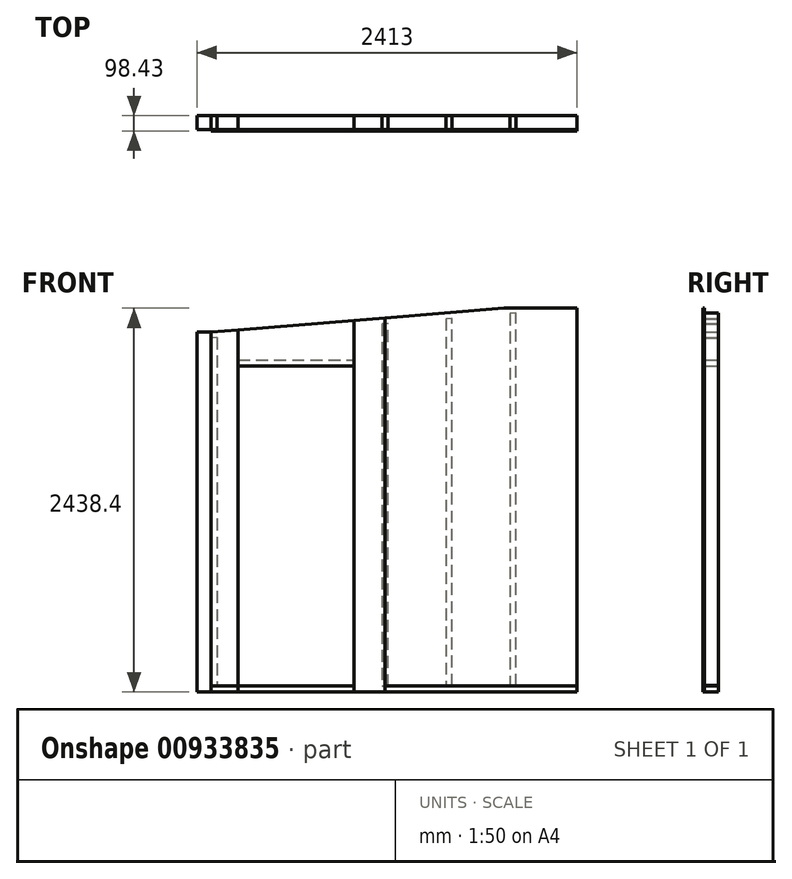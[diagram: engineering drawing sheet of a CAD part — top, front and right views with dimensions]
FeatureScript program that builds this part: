
annotation { "Feature Type Name" : "Feature", "Feature Type Description" : "" }
export const myFeature = defineFeature(function(context is Context, id is Id, definition is map)
    precondition{}
    {
        {
            var Q0;
            Q0=qCreatedBy(makeId("Front.planeOp"),FACE);
            var sketch = newSketch(context, id + "F0", { "sketchPlane" : qUnion([Q0])});
            skLineSegment(sketch, "E0.bottom", {"start": v(1162.05, -1238.25) * mm, "end": v(-1162.05, -1238.25) * mm, "construction": true});
            skLineSegment(sketch, "E0.left", {"start": v(1162.05, -1238.25) * mm, "end": v(1162.05, 1238.25) * mm, "construction": true});
            skPoint(sketch, "E0.middle", {"position": v(0, 0) * mm});
            skLineSegment(sketch, "E1.bottom", {"start": v(-1162.05, -1238.25) * mm, "end": v(1162.05, -1238.25) * mm});
            skLineSegment(sketch, "E1.top", {"start": v(-1162.05, -1200.15) * mm, "end": v(1162.05, -1200.15) * mm});
            skLineSegment(sketch, "E1.left", {"start": v(-1162.05, -1238.25) * mm, "end": v(-1162.05, -1200.15) * mm});
            skLineSegment(sketch, "E1.right", {"start": v(1162.05, -1238.25) * mm, "end": v(1162.05, -1200.15) * mm});
            skLineSegment(sketch, "E2", {"start": v(-1162.05, -1200.15) * mm, "end": v(-1162.05, 1047.75) * mm});
            skLineSegment(sketch, "E3", {"start": v(-1162.05, 1047.75) * mm, "end": v(-1162.05, -1200.15) * mm});
            skLineSegment(sketch, "E4.bottom", {"start": v(-1162.05, 1047.75) * mm, "end": v(-1250.95, 1047.75) * mm});
            skLineSegment(sketch, "E4.top", {"start": v(-1162.05, -1238.25) * mm, "end": v(-1250.95, -1238.25) * mm});
            skLineSegment(sketch, "E4.left", {"start": v(-1162.05, 1047.75) * mm, "end": v(-1162.05, -1238.25) * mm});
            skLineSegment(sketch, "E4.right", {"start": v(-1250.95, 1047.75) * mm, "end": v(-1250.95, -1238.25) * mm});
            skLineSegment(sketch, "E5", {"start": v(-1162.05, 1047.75) * mm, "end": v(1162.05, 1238.25) * mm, "construction": true});
            skLineSegment(sketch, "E6", {"start": v(-1162.05, 1009.52) * mm, "end": v(-1162.05, 1047.75) * mm});
            skLineSegment(sketch, "E7", {"start": v(-1162.05, 1047.75) * mm, "end": v(1162.05, 1238.25) * mm});
            skLineSegment(sketch, "E8", {"start": v(1162.05, 1238.25) * mm, "end": v(1162.05, 1200.02) * mm});
            skLineSegment(sketch, "E9", {"start": v(1162.05, 1200.02) * mm, "end": v(-1162.05, 1009.52) * mm});
            skLineSegment(sketch, "E10.bottom", {"start": v(-1162.05, -1200.15) * mm, "end": v(-1114.93, -1200.15) * mm});
            skLineSegment(sketch, "E10.left", {"start": v(-1162.05, -1200.15) * mm, "end": v(-1162.05, 1013.38) * mm});
            skLineSegment(sketch, "E11.bottom", {"start": v(1123.95, -1200.15) * mm, "end": v(1162.05, -1200.15) * mm});
            skLineSegment(sketch, "E11.top", {"start": v(1123.95, 1200.02) * mm, "end": v(1162.05, 1200.02) * mm});
            skLineSegment(sketch, "E11.left", {"start": v(1123.95, -1200.15) * mm, "end": v(1123.95, 1200.02) * mm});
            skLineSegment(sketch, "E11.right", {"start": v(1162.05, -1200.15) * mm, "end": v(1162.05, 1200.02) * mm});
            skLineSegment(sketch, "E12", {"start": v(-1123.95, 1012.65) * mm, "end": v(-1123.95, -1200.15) * mm});
            skLineSegment(sketch, "E13", {"start": v(-1123.95, -1200.15) * mm, "end": v(-1162.05, -1200.15) * mm});
            skLineSegment(sketch, "E14.bottom", {"start": v(-1028.7, 1339.8) * mm, "end": v(-990.6, 1339.8) * mm, "construction": true});
            skLineSegment(sketch, "E14.top", {"start": v(-1028.7, -2064.35) * mm, "end": v(-990.6, -2064.35) * mm, "construction": true});
            skLineSegment(sketch, "E14.left", {"start": v(-1028.7, 1339.8) * mm, "end": v(-1028.7, -2064.35) * mm, "construction": true});
            skLineSegment(sketch, "E14.right", {"start": v(-990.6, 1339.8) * mm, "end": v(-990.6, -2064.35) * mm, "construction": true});
            skLineSegment(sketch, "E15.bottom", {"start": v(-254, 1339.8) * mm, "end": v(-215.9, 1339.8) * mm, "construction": true});
            skLineSegment(sketch, "E15.top", {"start": v(-254, -1935.77) * mm, "end": v(-215.9, -1935.77) * mm, "construction": true});
            skLineSegment(sketch, "E15.left", {"start": v(-254, 1339.8) * mm, "end": v(-254, -1935.77) * mm, "construction": true});
            skLineSegment(sketch, "E15.right", {"start": v(-215.9, 1339.8) * mm, "end": v(-215.9, -1935.77) * mm, "construction": true});
            skLineSegment(sketch, "E16", {"start": v(-990.6, 1023.58) * mm, "end": v(-990.6, -1200.15) * mm});
            skLineSegment(sketch, "E17", {"start": v(-990.6, -1200.15) * mm, "end": v(-1028.7, -1200.15) * mm});
            skLineSegment(sketch, "E18", {"start": v(-1028.7, -1200.15) * mm, "end": v(-1028.7, 1020.45) * mm});
            skLineSegment(sketch, "E19", {"start": v(-1028.7, 1020.45) * mm, "end": v(-990.6, 1023.58) * mm});
            skLineSegment(sketch, "E20", {"start": v(-254, 1083.95) * mm, "end": v(-254, -1200.15) * mm});
            skLineSegment(sketch, "E21", {"start": v(-254, -1200.15) * mm, "end": v(-215.9, -1200.15) * mm});
            skLineSegment(sketch, "E22", {"start": v(-215.9, -1200.15) * mm, "end": v(-215.9, 1087.08) * mm});
            skLineSegment(sketch, "E23", {"start": v(-215.9, 1087.08) * mm, "end": v(-254, 1083.95) * mm});
            skLineSegment(sketch, "E24.bottom", {"start": v(-76.2, 1404.76) * mm, "end": v(-38.1, 1404.76) * mm, "construction": true});
            skLineSegment(sketch, "E24.top", {"start": v(-76.2, -1704.93) * mm, "end": v(-38.1, -1704.93) * mm, "construction": true});
            skLineSegment(sketch, "E24.left", {"start": v(-76.2, 1404.76) * mm, "end": v(-76.2, -1704.93) * mm, "construction": true});
            skLineSegment(sketch, "E24.right", {"start": v(-38.1, 1404.76) * mm, "end": v(-38.1, -1704.93) * mm, "construction": true});
            skLineSegment(sketch, "E25.1.0.0", {"start": v(368.3, 1404.76) * mm, "end": v(368.3, -1704.93) * mm, "construction": true});
            skLineSegment(sketch, "E25.1.0.1", {"start": v(330.2, 1404.76) * mm, "end": v(330.2, -1704.93) * mm, "construction": true});
            skLineSegment(sketch, "E25.2.0.0", {"start": v(774.7, 1404.76) * mm, "end": v(774.7, -1704.93) * mm, "construction": true});
            skLineSegment(sketch, "E25.2.0.1", {"start": v(736.6, 1404.76) * mm, "end": v(736.6, -1704.93) * mm, "construction": true});
            skLineSegment(sketch, "E25.direction1", {"start": v(-38.1, -1704.93) * mm, "end": v(368.3, -1704.93) * mm, "construction": true});
            skLineSegment(sketch, "E26", {"start": v(-76.2, 1098.53) * mm, "end": v(-76.2, -1200.15) * mm});
            skLineSegment(sketch, "E27", {"start": v(-76.2, -1200.15) * mm, "end": v(-38.1, -1200.15) * mm});
            skLineSegment(sketch, "E28", {"start": v(-38.1, -1200.15) * mm, "end": v(-38.1, 1101.65) * mm});
            skLineSegment(sketch, "E29", {"start": v(-38.1, 1101.65) * mm, "end": v(-76.2, 1098.53) * mm});
            skLineSegment(sketch, "E30", {"start": v(330.2, 1131.84) * mm, "end": v(330.2, -1200.15) * mm});
            skLineSegment(sketch, "E31", {"start": v(330.2, -1200.15) * mm, "end": v(368.3, -1197.03) * mm});
            skLineSegment(sketch, "E32", {"start": v(368.3, -1197.03) * mm, "end": v(368.3, 1134.96) * mm});
            skLineSegment(sketch, "E33", {"start": v(368.3, 1134.96) * mm, "end": v(330.2, 1131.84) * mm});
            skLineSegment(sketch, "E34", {"start": v(736.6, 1165.15) * mm, "end": v(736.6, -1200.15) * mm});
            skLineSegment(sketch, "E35", {"start": v(736.6, -1200.15) * mm, "end": v(774.7, -1197.03) * mm});
            skLineSegment(sketch, "E36", {"start": v(774.7, -1197.03) * mm, "end": v(774.7, 1168.27) * mm});
            skLineSegment(sketch, "E37", {"start": v(774.7, 1168.27) * mm, "end": v(736.6, 1165.15) * mm});
            skLineSegment(sketch, "E38.bottom", {"start": v(-990.6, 869.95) * mm, "end": v(-254, 869.95) * mm});
            skLineSegment(sketch, "E38.top", {"start": v(-990.6, 831.85) * mm, "end": v(-254, 831.85) * mm});
            skLineSegment(sketch, "E38.left", {"start": v(-990.6, 869.95) * mm, "end": v(-990.6, 831.85) * mm});
            skLineSegment(sketch, "E38.right", {"start": v(-254, 869.95) * mm, "end": v(-254, 831.85) * mm});
            skSolve(sketch);
        }
        {
            var Q0;
            Q0=makeQuery(id+"F0.imprint","IMPRINT",FACE,{"disambiguationData":[TD([[makeQuery(id+"F0.imprint","IMPRINT",EDGE,{"derivedFrom":sQuery(id+"F0.wireOp",EDGE,"E4.bottom")}),1.0]])]});
            var Q1;
            {var subQ0=sQuery(id+"F0.wireOp",EDGE,"E17");Q1=makeQuery(id+"F0.imprint","IMPRINT",FACE,{"disambiguationData":[TD([[makeQuery(id+"F0.imprint","IMPRINT",EDGE,{"derivedFrom":subQ0}),-1.0]])]});}
            var Q2;
            {var subQ0=sQuery(id+"F0.wireOp",EDGE,"E21");Q2=makeQuery(id+"F0.imprint","IMPRINT",FACE,{"disambiguationData":[TD([[makeQuery(id+"F0.imprint","IMPRINT",EDGE,{"derivedFrom":subQ0}),1.0]])]});}
            var Q3;
            Q3=makeQuery(id+"F0.imprint","IMPRINT",FACE,{"disambiguationData":[TD([[makeQuery(id+"F0.imprint","IMPRINT",EDGE,{"derivedFrom":sQuery(id+"F0.wireOp",EDGE,"E26")}),1.0]])]});
            var Q4;
            Q4=makeQuery(id+"F0.imprint","IMPRINT",FACE,{"disambiguationData":[TD([[makeQuery(id+"F0.imprint","IMPRINT",EDGE,{"derivedFrom":sQuery(id+"F0.wireOp",EDGE,"E30")}),1.0]])]});
            var Q5;
            Q5=makeQuery(id+"F0.imprint","IMPRINT",FACE,{"disambiguationData":[TD([[makeQuery(id+"F0.imprint","IMPRINT",EDGE,{"derivedFrom":sQuery(id+"F0.wireOp",EDGE,"E34")}),1.0]])]});
            var Q6;
            {var subQ4=sQuery(id+"F0.wireOp",EDGE,"E11.bottom");Q6=makeQuery(id+"F0.imprint","IMPRINT",FACE,{"disambiguationData":[TD([[makeQuery(id+"F0.imprint","IMPRINT",EDGE,{"derivedFrom":subQ4}),1.0]])]});}
            extrude(context, id + "F1", {"entities" : qUnion([Q0, Q1, Q2, Q3, Q4, Q5, Q6]), "endBound" : BoundingType.SYMMETRIC, "depth" : 88.9 * mm, "offsetDistance" : 25.4 * mm});
        }
        {
            var Q0;
            {var subQ9=sQuery(id+"F0.wireOp",EDGE,"E6");Q0=makeQuery(id+"F0.imprint","IMPRINT",FACE,{"disambiguationData":[TD([[makeQuery(id+"F0.imprint","IMPRINT",EDGE,{"derivedFrom":subQ9}),-1.0]])]});}
            var Q1;
            Q1=makeQuery(id+"F0.imprint","IMPRINT",FACE,{"disambiguationData":[TD([[makeQuery(id+"F0.imprint","IMPRINT",EDGE,{"derivedFrom":sQuery(id+"F0.wireOp",EDGE,"E38.bottom")}),-1.0]])]});
            var Q2;
            Q2=makeQuery(id+"F0.imprint","IMPRINT",FACE,{"disambiguationData":[TD([[makeQuery(id+"F0.imprint","IMPRINT",EDGE,{"derivedFrom":sQuery(id+"F0.wireOp",EDGE,"E1.bottom")}),1.0]])]});
            extrude(context, id + "F2", {"entities" : qUnion([Q0, Q1, Q2]), "endBound" : BoundingType.SYMMETRIC, "depth" : 88.9 * mm, "offsetDistance" : 25.4 * mm});
        }
        {
            var Q0;
            {var subQ3=sQuery(id+"F0.wireOp",EDGE,"E12");Q0=makeQuery(id+"F0.imprint","IMPRINT",FACE,{"disambiguationData":[TD([[makeQuery(id+"F0.imprint","IMPRINT",EDGE,{"derivedFrom":subQ3}),-1.0]])]});}
            extrude(context, id + "F3", {"entities" : qUnion([Q0]), "endBound" : BoundingType.SYMMETRIC, "depth" : 88.9 * mm, "offsetDistance" : 25.4 * mm});
        }
        {
            var Q0;
            Q0=makeQuery(id+"F2.opExtrude","CAP_FACE",FACE,{"disambiguationData":[OSD([sQuery(id+"F0.wireOp",EDGE,"E1.bottom"),sQuery(id+"F0.wireOp",EDGE,"E1.top"),sQuery(id+"F0.wireOp",EDGE,"E1.right"),sQuery(id+"F0.wireOp",EDGE,"E4.left"),sQuery(id+"F0.wireOp",EDGE,"E10.bottom"),sQuery(id+"F0.wireOp",EDGE,"E11.bottom"),sQuery(id+"F0.wireOp",EDGE,"E13"),sQuery(id+"F0.wireOp",EDGE,"E17"),sQuery(id+"F0.wireOp",EDGE,"E21"),sQuery(id+"F0.wireOp",EDGE,"E27")])],"isStart":false});
            var sketch = newSketch(context, id + "F4", { "sketchPlane" : qUnion([Q0])});
            skLineSegment(sketch, "E39.bottom", {"start": v(1162.05, -1238.25) * mm, "end": v(-57.15, -1238.25) * mm});
            skLineSegment(sketch, "E39.top", {"start": v(1162.05, 1200.15) * mm, "end": v(-57.15, 1200.15) * mm});
            skLineSegment(sketch, "E39.left", {"start": v(1162.05, -1238.25) * mm, "end": v(1162.05, 1200.15) * mm});
            skLineSegment(sketch, "E39.right", {"start": v(-57.15, -1238.25) * mm, "end": v(-57.15, 1200.15) * mm});
            skLineSegment(sketch, "E40.0", {"start": v(-1162.05, 1047.75) * mm, "end": v(1162.05, 1238.25) * mm});
            skLineSegment(sketch, "E41.0", {"start": v(-990.6, 1023.58) * mm, "end": v(-990.6, -1200.15) * mm});
            skLineSegment(sketch, "E42.0", {"start": v(-254, 1083.95) * mm, "end": v(-254, -1200.15) * mm});
            skLineSegment(sketch, "E43.0", {"start": v(-990.6, 831.85) * mm, "end": v(-254, 831.85) * mm});
            skLineSegment(sketch, "E44.0", {"start": v(-1162.05, -1238.25) * mm, "end": v(1162.05, -1238.25) * mm});
            skLineSegment(sketch, "E45.0", {"start": v(-1162.05, 1047.75) * mm, "end": v(-1162.05, -1238.25) * mm});
            skLineSegment(sketch, "E46", {"start": v(-990.6, 831.85) * mm, "end": v(-990.6, 1061.8) * mm});
            skLineSegment(sketch, "E47", {"start": v(-990.6, 1061.8) * mm, "end": v(-254, 1122.18) * mm});
            skLineSegment(sketch, "E48", {"start": v(-254, 1122.18) * mm, "end": v(-254, 831.85) * mm});
            skLineSegment(sketch, "E49", {"start": v(-990.6, -1200.15) * mm, "end": v(-990.6, -1238.25) * mm});
            skLineSegment(sketch, "E50", {"start": v(-990.6, -1238.25) * mm, "end": v(-254, -1238.25) * mm});
            skLineSegment(sketch, "E51", {"start": v(-254, -1238.25) * mm, "end": v(-254, -1200.15) * mm});
            skSolve(sketch);
        }
        {
            var Q0;
            {var subQ1=sQuery(id+"F4.wireOp",EDGE,"E41.0");Q0=makeQuery(id+"F4.imprint","IMPRINT",FACE,{"disambiguationData":[TD([[makeQuery(id+"F4.imprint","IMPRINT",EDGE,{"derivedFrom":subQ1}),-1.0]])]});}
            var Q1;
            {var subQ4=sQuery(id+"F4.wireOp",EDGE,"E42.0");Q1=makeQuery(id+"F4.imprint","IMPRINT",FACE,{"disambiguationData":[TD([[makeQuery(id+"F4.imprint","IMPRINT",EDGE,{"derivedFrom":subQ4}),1.0]])]});}
            var Q2;
            {var subQ3=sQuery(id+"F4.wireOp",EDGE,"E49");Q2=makeQuery(id+"F4.imprint","IMPRINT",FACE,{"disambiguationData":[TD([[makeQuery(id+"F4.imprint","IMPRINT",EDGE,{"derivedFrom":subQ3}),-1.0]])]});}
            var Q3;
            {var subQ5=sQuery(id+"F4.wireOp",EDGE,"E51");Q3=makeQuery(id+"F4.imprint","IMPRINT",FACE,{"disambiguationData":[TD([[makeQuery(id+"F4.imprint","IMPRINT",EDGE,{"derivedFrom":subQ5}),-1.0]])]});}
            extrude(context, id + "F5", {"entities" : qUnion([Q0, Q1, Q2, Q3]), "depth" : 9.52 * mm, "offsetDistance" : 25.4 * mm});
        }
        {
            var Q0;
            {var subQ4=sQuery(id+"F4.wireOp",EDGE,"E43.0");Q0=makeQuery(id+"F4.imprint","IMPRINT",FACE,{"disambiguationData":[TD([[makeQuery(id+"F4.imprint","IMPRINT",EDGE,{"derivedFrom":subQ4}),1.0]])]});}
            var Q1;
            {var subQ1=sQuery(id+"F4.wireOp",EDGE,"E39.top");var subQ5=sQuery(id+"F4.wireOp",EDGE,"E39.left");var subQ8=makeQuery(id+"F4.imprint","INTERSECT",VERTEX,{"derivedFrom":[subQ1,subQ5]});Q1=makeQuery(id+"F4.imprint","IMPRINT",FACE,{"disambiguationData":[TD([[makeQuery(id+"F4.imprint","IMPRINT",EDGE,{"disambiguationData":[TD([[subQ8,-1.0]])],"derivedFrom":subQ1}),1.0]])]});}
            var Q2;
            {var subQ0=sQuery(id+"F4.wireOp",EDGE,"E44.0");var subQ1=sQuery(id+"F4.wireOp",EDGE,"E39.left");var subQ2=makeQuery(id+"F4.imprint","INTERSECT",VERTEX,{"derivedFrom":[subQ1,subQ0]});Q2=makeQuery(id+"F4.imprint","IMPRINT",FACE,{"disambiguationData":[TD([[makeQuery(id+"F4.imprint","IMPRINT",EDGE,{"disambiguationData":[TD([[subQ2,1.0]])],"derivedFrom":subQ0}),1.0]])]});}
            extrude(context, id + "F6", {"entities" : qUnion([Q0, Q1, Q2]), "depth" : 9.52 * mm, "offsetDistance" : 25.4 * mm});
        }
    });
